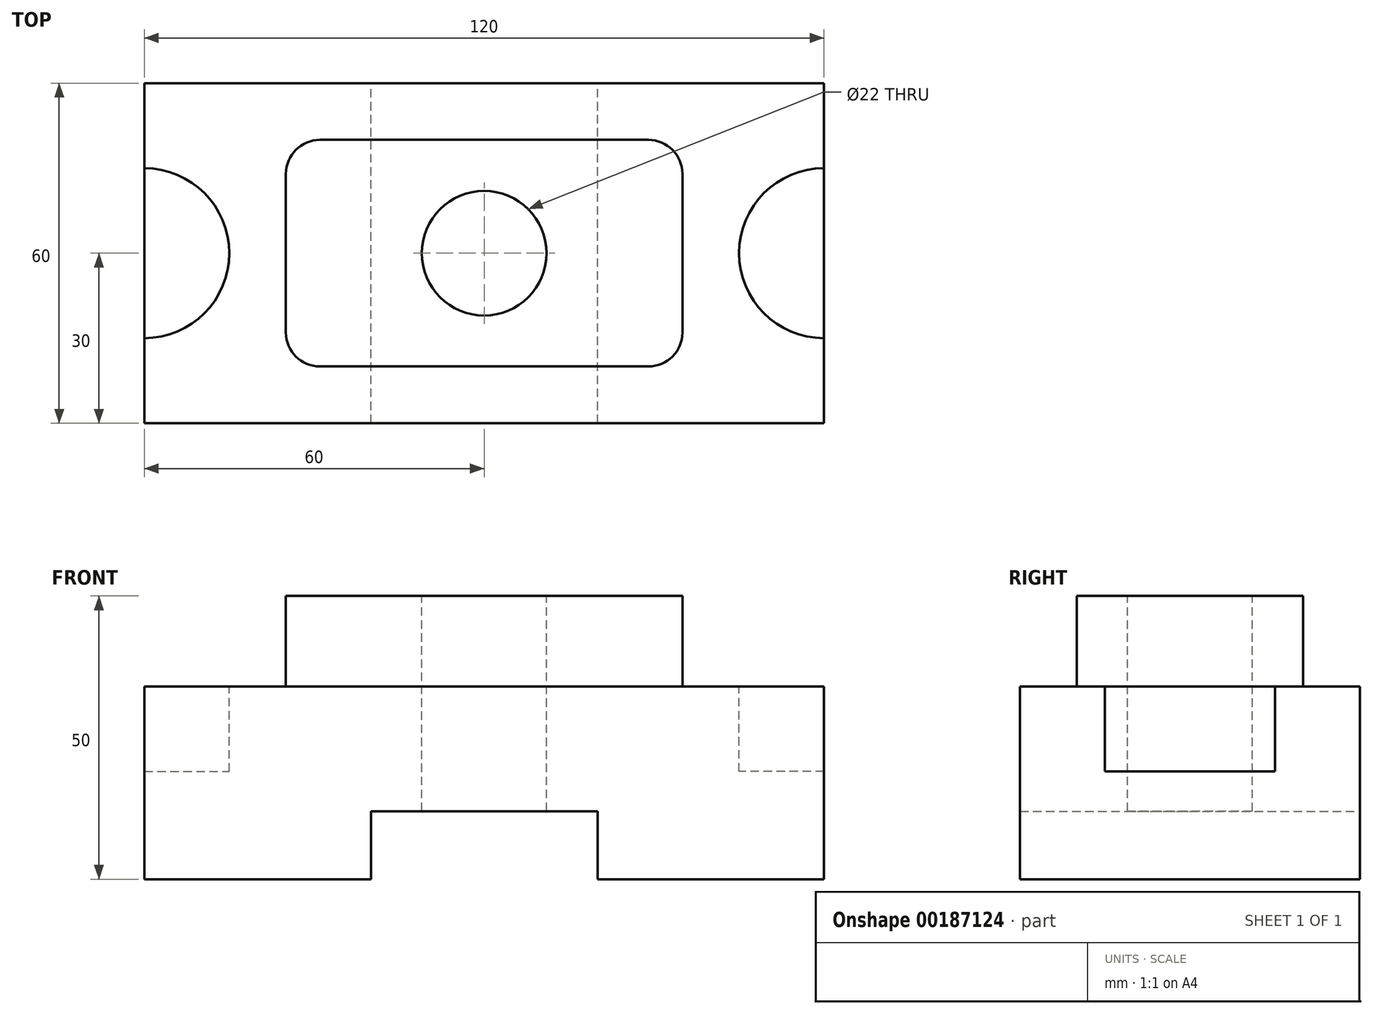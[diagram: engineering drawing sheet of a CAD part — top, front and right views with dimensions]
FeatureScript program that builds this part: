
annotation { "Feature Type Name" : "Feature", "Feature Type Description" : "" }
export const myFeature = defineFeature(function(context is Context, id is Id, definition is map)
    precondition{}
    {
        {
            var Q0;
            Q0=qCreatedBy(makeId("Top.planeOp"),FACE);
            var sketch = newSketch(context, id + "F0", { "sketchPlane" : qUnion([Q0])});
            skLineSegment(sketch, "E0.bottom", {"start": v(60, 30) * mm, "end": v(-60, 30) * mm});
            skLineSegment(sketch, "E0.top", {"start": v(60, -30) * mm, "end": v(-60, -30) * mm});
            skLineSegment(sketch, "E0.left", {"start": v(60, 30) * mm, "end": v(60, -30) * mm});
            skLineSegment(sketch, "E0.right", {"start": v(-60, 30) * mm, "end": v(-60, -30) * mm});
            skPoint(sketch, "E0.middle", {"position": v(0, 0) * mm});
            skSolve(sketch);
        }
        {
            var Q0;
            Q0 = qSketchRegion(id + "F0", true);
            extrude(context, id + "F1", {"entities" : qUnion([Q0]), "depth" : 34 * mm});
        }
        {
            var Q0;
            Q0=makeQuery(id+"F1.opExtrude","CAP_FACE",FACE,{"disambiguationData":[OSD([sQuery(id+"F0.wireOp",EDGE,"E0.bottom"),sQuery(id+"F0.wireOp",EDGE,"E0.top"),sQuery(id+"F0.wireOp",EDGE,"E0.left"),sQuery(id+"F0.wireOp",EDGE,"E0.right")])],"isStart":false});
            var sketch = newSketch(context, id + "F2", { "sketchPlane" : qUnion([Q0])});
            skArc(sketch, "E1", {"start": v(60, 15) * mm, "mid": v(45, 0) * mm, "end": v(60, -15) * mm});
            skArc(sketch, "E2", {"start": v(-60, -15) * mm, "mid": v(-45, 0) * mm, "end": v(-60, 15) * mm});
            skSolve(sketch);
        }
        {
            var Q0;
            {var subQ0=sQuery(id+"F2.wireOp",EDGE,"E2");Q0=makeQuery(id+"F2.imprint","IMPRINT",FACE,{"disambiguationData":[TD([[makeQuery(id+"F2.imprint","IMPRINT",EDGE,{"derivedFrom":subQ0}),1.0]])]});}
            var Q1;
            {var subQ0=sQuery(id+"F2.wireOp",EDGE,"E1");Q1=makeQuery(id+"F2.imprint","IMPRINT",FACE,{"disambiguationData":[TD([[makeQuery(id+"F2.imprint","IMPRINT",EDGE,{"derivedFrom":subQ0}),1.0]])]});}
            extrude(context, id + "F3", {"entities" : qUnion([Q0, Q1]), "operationType" : NewBodyOperationType.REMOVE, "oppositeDirection" : true, "depth" : 15 * mm});
        }
        {
            var Q0;
            Q0=makeQuery(id+"F1.opExtrude","CAP_FACE",FACE,{"disambiguationData":[OSD([sQuery(id+"F0.wireOp",EDGE,"E0.bottom"),sQuery(id+"F0.wireOp",EDGE,"E0.top"),sQuery(id+"F0.wireOp",EDGE,"E0.left"),sQuery(id+"F0.wireOp",EDGE,"E0.right")])],"isStart":false});
            var sketch = newSketch(context, id + "F4", { "sketchPlane" : qUnion([Q0])});
            skLineSegment(sketch, "E3.bottom", {"start": v(-35, 20) * mm, "end": v(35, 20) * mm});
            skLineSegment(sketch, "E3.top", {"start": v(-35, -20) * mm, "end": v(35, -20) * mm});
            skLineSegment(sketch, "E3.left", {"start": v(-35, 20) * mm, "end": v(-35, -20) * mm});
            skLineSegment(sketch, "E3.right", {"start": v(35, 20) * mm, "end": v(35, -20) * mm});
            skPoint(sketch, "E3.middle", {"position": v(0, 0) * mm});
            skSolve(sketch);
        }
        {
            var Q0;
            Q0=makeQuery(id+"F4.imprint","IMPRINT",FACE,{"disambiguationData":[TD([[makeQuery(id+"F4.imprint","IMPRINT",EDGE,{"derivedFrom":sQuery(id+"F4.wireOp",EDGE,"E3.bottom")}),-1.0]])]});
            extrude(context, id + "F5", {"entities" : qUnion([Q0]), "operationType" : NewBodyOperationType.ADD, "depth" : 16 * mm});
        }
        {
            var Q0;
            Q0=makeQuery(id+"F5.opExtrude","CAP_FACE",FACE,{"disambiguationData":[OSD([sQuery(id+"F4.wireOp",EDGE,"E3.bottom"),sQuery(id+"F4.wireOp",EDGE,"E3.top"),sQuery(id+"F4.wireOp",EDGE,"E3.left"),sQuery(id+"F4.wireOp",EDGE,"E3.right")])],"isStart":false});
            var sketch = newSketch(context, id + "F6", { "sketchPlane" : qUnion([Q0])});
            skCircle(sketch, "E4", {"center": v(0, 0) * mm, "radius": 11 * mm});
            skSolve(sketch);
        }
        {
            var Q0;
            Q0 = qSketchRegion(id + "F6", true);
            extrude(context, id + "F7", {"entities" : qUnion([Q0]), "operationType" : NewBodyOperationType.REMOVE, "endBound" : BoundingType.THROUGH_ALL, "oppositeDirection" : true, "depth" : 25 * mm});
        }
        {
            var Q0;
            Q0=makeQuery(id+"F5.opExtrude","SWEPT_EDGE",EDGE,{"disambiguationData":[OSD([sQuery(id+"F4.wireOp",EDGE,"E3.bottom"),sQuery(id+"F4.wireOp",EDGE,"E3.right")])]});
            var Q1;
            Q1=makeQuery(id+"F5.opExtrude","SWEPT_EDGE",EDGE,{"disambiguationData":[OSD([sQuery(id+"F4.wireOp",EDGE,"E3.bottom"),sQuery(id+"F4.wireOp",EDGE,"E3.left")])]});
            var Q2;
            Q2=makeQuery(id+"F5.opExtrude","SWEPT_EDGE",EDGE,{"disambiguationData":[OSD([sQuery(id+"F4.wireOp",EDGE,"E3.top"),sQuery(id+"F4.wireOp",EDGE,"E3.left")])]});
            var Q3;
            Q3=makeQuery(id+"F5.opExtrude","SWEPT_EDGE",EDGE,{"disambiguationData":[OSD([sQuery(id+"F4.wireOp",EDGE,"E3.top"),sQuery(id+"F4.wireOp",EDGE,"E3.right")])]});
            fillet(context, id + "F8", {"entities" : qUnion([Q0, Q1, Q2, Q3]), "radius" : 6 * mm, "tangentPropagation" : true, "allowEdgeOverflow" : false});
        }
        {
            var Q0;
            Q0=makeQuery(id+"F1.opExtrude","SWEPT_FACE",FACE,{"disambiguationData":[OSD([sQuery(id+"F0.wireOp",EDGE,"E0.bottom")])]});
            var sketch = newSketch(context, id + "F9", { "sketchPlane" : qUnion([Q0])});
            skLineSegment(sketch, "E5.bottom", {"start": v(20, 12) * mm, "end": v(-20, 12) * mm});
            skLineSegment(sketch, "E5.top", {"start": v(20, -12) * mm, "end": v(-20, -12) * mm});
            skLineSegment(sketch, "E5.left", {"start": v(20, 12) * mm, "end": v(20, -12) * mm});
            skLineSegment(sketch, "E5.right", {"start": v(-20, 12) * mm, "end": v(-20, -12) * mm});
            skPoint(sketch, "E5.middle", {"position": v(0, 0) * mm});
            skSolve(sketch);
        }
        {
            var Q0;
            Q0 = qSketchRegion(id + "F9", true);
            extrude(context, id + "F10", {"entities" : qUnion([Q0]), "operationType" : NewBodyOperationType.REMOVE, "endBound" : BoundingType.THROUGH_ALL, "oppositeDirection" : true, "depth" : 25 * mm});
        }
    });
